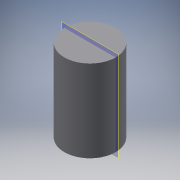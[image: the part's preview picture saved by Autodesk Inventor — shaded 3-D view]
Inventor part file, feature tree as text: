
AUTODESK INVENTOR PART (.ipt)
format: ipt  version: 2016 (Build 200138000, 138)  size: 94,720 bytes
history: native  units: mm
features: extrude x2, sketch x2
ambient origin geometry x8: Origin, YZ Plane, XZ Plane, XY Plane, X Axis, Y Axis, Z Axis, Center Point
bodies: Solid1 (feature_tree)
feature tree (4):
  extrude  "Extrusion1"  Depth=80.0mm TaperAngle=0.0deg
  extrude  "Extrusion2"  Depth=60.0mm TaperAngle=0.0deg
  sketch  "Sketch1"  dims[d0=50.0mm d1=80.0mm d2=0.0mm]
  sketch  "Sketch2"  dims[d3=40.0mm d4=60.0mm d5=0.0mm]
